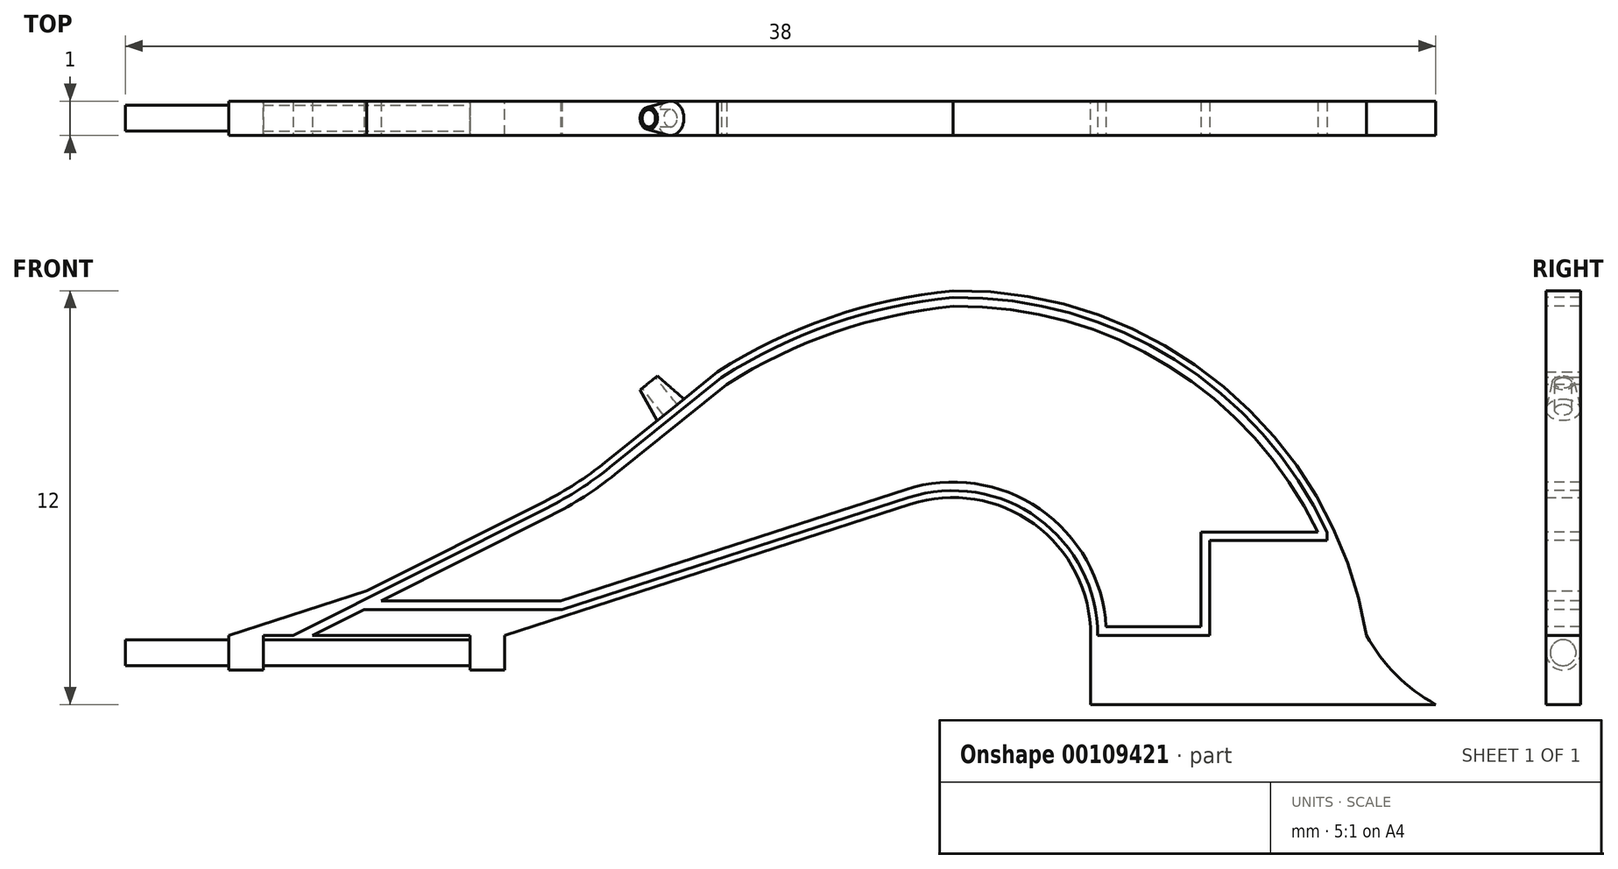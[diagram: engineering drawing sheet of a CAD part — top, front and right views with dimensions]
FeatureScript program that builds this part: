
annotation { "Feature Type Name" : "Feature", "Feature Type Description" : "" }
export const myFeature = defineFeature(function(context is Context, id is Id, definition is map)
    precondition{}
    {
        {
            var Q0;
            Q0=qCreatedBy(makeId("Front.planeOp"),FACE);
            var sketch = newSketch(context, id + "F0", { "sketchPlane" : qUnion([Q0])});
            skArc(sketch, "E0", {"start": v(4, 0) * mm, "mid": v(2.35, 3.23) * mm, "end": v(-1.23, 3.8) * mm});
            skLineSegment(sketch, "E1", {"start": v(-13, 0) * mm, "end": v(-1.23, 3.8) * mm});
            skLineSegment(sketch, "E2", {"start": v(-13, 0) * mm, "end": v(-21, 0) * mm});
            skLineSegment(sketch, "E3", {"start": v(-21, 0) * mm, "end": v(-17, 1.3) * mm});
            skArc(sketch, "E4", {"start": v(12, 0) * mm, "mid": v(7.85, 7.22) * mm, "end": v(0, 10) * mm});
            skLineSegment(sketch, "E5.left", {"start": v(4, 0) * mm, "end": v(4, -2) * mm});
            skPoint(sketch, "E6.visualSharp", {"position": v(-17, 1.3) * mm});
            skArc(sketch, "E7", {"start": v(12, 0) * mm, "mid": v(12.86, -1.14) * mm, "end": v(14, -2) * mm});
            skLineSegment(sketch, "E8", {"start": v(4, -2) * mm, "end": v(14, -2) * mm});
            skLineSegment(sketch, "E9", {"start": v(-17, 1.3) * mm, "end": v(-11.86, 3.88) * mm});
            skLineSegment(sketch, "E10", {"start": v(-10.08, 5.03) * mm, "end": v(-6.83, 7.65) * mm});
            skPoint(sketch, "E11.visualSharp", {"position": v(-10.9, 4.36) * mm});
            skArc(sketch, "E11.filletArc", {"start": v(-11.86, 3.88) * mm, "mid": v(-10.94, 4.4) * mm, "end": v(-10.08, 5.03) * mm});
            skArc(sketch, "E12", {"start": v(0, 10) * mm, "mid": v(-3.55, 9.23) * mm, "end": v(-6.83, 7.65) * mm});
            skSolve(sketch);
        }
        {
            var Q0;
            Q0 = qSketchRegion(id + "F0", true);
            extrude(context, id + "F1", {"entities" : qUnion([Q0]), "depth" : 1 * mm, "offsetDistance" : 25 * mm});
        }
        {
            var Q0;
            Q0=makeQuery(id+"F1.opExtrude","SWEPT_FACE",FACE,{"disambiguationData":[OSD([sQuery(id+"F0.wireOp",EDGE,"E2")])]});
            var sketch = newSketch(context, id + "F2", { "sketchPlane" : qUnion([Q0])});
            skLineSegment(sketch, "E13.bottom", {"start": v(-13, 1) * mm, "end": v(-14, 1) * mm});
            skLineSegment(sketch, "E13.top", {"start": v(-13, 0) * mm, "end": v(-14, 0) * mm});
            skLineSegment(sketch, "E13.left", {"start": v(-13, 1) * mm, "end": v(-13, 0) * mm});
            skLineSegment(sketch, "E13.right", {"start": v(-14, 1) * mm, "end": v(-14, 0) * mm});
            skSolve(sketch);
        }
        {
            var Q0;
            Q0 = qSketchRegion(id + "F2", true);
            extrude(context, id + "F3", {"entities" : qUnion([Q0]), "operationType" : NewBodyOperationType.ADD, "depth" : 1 * mm});
        }
        {
            var Q0;
            Q0=makeQuery(id+"F3.opExtrude","SWEPT_FACE",FACE,{"disambiguationData":[OSD([sQuery(id+"F2.wireOp",EDGE,"E13.right")])]});
            var sketch = newSketch(context, id + "F4", { "sketchPlane" : qUnion([Q0])});
            skLineSegment(sketch, "E14.top", {"start": v(0.5, -1) * mm, "end": v(0.5, -1) * mm});
            skLineSegment(sketch, "E14.left", {"start": v(0, 0) * mm, "end": v(0, -0.5) * mm});
            skLineSegment(sketch, "E14.right", {"start": v(1, 0) * mm, "end": v(1, -0.5) * mm});
            skPoint(sketch, "E15.visualSharp", {"position": v(0, -1) * mm});
            skArc(sketch, "E15.filletArc", {"start": v(0, -0.5) * mm, "mid": v(0.15, -0.85) * mm, "end": v(0.5, -1) * mm});
            skPoint(sketch, "E16.visualSharp", {"position": v(1, -1) * mm});
            skArc(sketch, "E16.filletArc", {"start": v(0.5, -1) * mm, "mid": v(0.85, -0.85) * mm, "end": v(1, -0.5) * mm});
            skLineSegment(sketch, "E17", {"start": v(0, 0) * mm, "end": v(-0.43, 0) * mm});
            skLineSegment(sketch, "E18", {"start": v(-0.43, 0) * mm, "end": v(-0.43, -1) * mm});
            skLineSegment(sketch, "E19", {"start": v(1, 0) * mm, "end": v(1.47, 0) * mm});
            skLineSegment(sketch, "E20", {"start": v(1.47, 0) * mm, "end": v(1.47, -1) * mm});
            skLineSegment(sketch, "E21", {"start": v(-0.43, -1) * mm, "end": v(0.5, -1.26) * mm});
            skLineSegment(sketch, "E22", {"start": v(0.5, -1.26) * mm, "end": v(1.47, -1) * mm});
            skLineSegment(sketch, "E23", {"start": v(1, -0.5) * mm, "end": v(1, 0) * mm});
            skLineSegment(sketch, "E24", {"start": v(0, -0.5) * mm, "end": v(0, 0) * mm});
            skSolve(sketch);
        }
        {
            var Q0;
            Q0 = qSketchRegion(id + "F4", true);
            extrude(context, id + "F5", {"entities" : qUnion([Q0]), "operationType" : NewBodyOperationType.REMOVE, "oppositeDirection" : true, "depth" : 1.1 * mm});
        }
        {
            var Q0;
            Q0=makeQuery(id+"F3.opExtrude","SWEPT_FACE",FACE,{"disambiguationData":[OSD([sQuery(id+"F2.wireOp",EDGE,"E13.right")])]});
            var sketch = newSketch(context, id + "F6", { "sketchPlane" : qUnion([Q0])});
            skCircle(sketch, "E25", {"center": v(0.5, -0.5) * mm, "radius": 0.5 * mm});
            skSolve(sketch);
        }
        {
            var Q0;
            Q0 = qSketchRegion(id + "F6", true);
            extrude(context, id + "F7", {"entities" : qUnion([Q0]), "depth" : 10 * mm});
        }
        {
            var Q0;
            Q0=makeQuery(id+"F1.opExtrude","SWEPT_FACE",FACE,{"disambiguationData":[OSD([sQuery(id+"F0.wireOp",EDGE,"E10")])]});
            var sketch = newSketch(context, id + "F8", { "sketchPlane" : qUnion([Q0])});
            skCircle(sketch, "E26", {"center": v(-2.27, -0.5) * mm, "radius": 0.5 * mm});
            skSolve(sketch);
        }
        {
            var Q0;
            Q0 = qSketchRegion(id + "F8", true);
            extrude(context, id + "F9", {"entities" : qUnion([Q0]), "operationType" : NewBodyOperationType.ADD, "depth" : 1 * mm, "hasDraft" : true, "draftAngle" : 10 * degree, "draftPullDirection" : true});
        }
        {
            var Q0;
            Q0=makeQuery(id+"F9.opExtrude","CAP_FACE",FACE,{"disambiguationData":[OSD([sQuery(id+"F8.wireOp",EDGE,"E26")])],"isStart":false});
            var sketch = newSketch(context, id + "F10", { "sketchPlane" : qUnion([Q0])});
            skCircle(sketch, "E27", {"center": v(-2.27, -0.5) * mm, "radius": 0.25 * mm});
            skSolve(sketch);
        }
        {
            var Q0;
            Q0=makeQuery(id+"F10.imprint","IMPRINT",FACE,{"disambiguationData":[TD([[makeQuery(id+"F10.imprint","IMPRINT",EDGE,{"derivedFrom":sQuery(id+"F10.wireOp",EDGE,"E27")}),1.0]])]});
            extrude(context, id + "F11", {"entities" : qUnion([Q0]), "operationType" : NewBodyOperationType.REMOVE, "oppositeDirection" : true, "depth" : 1 * mm});
        }
        {
            var Q0;
            Q0=makeQuery(id+"F7.opExtrude","SWEPT_BODY",BODY,{"disambiguationData":[OSD([sQuery(id+"F6.wireOp",EDGE,"E25")])]});
            deleteBodies(context, id + "F12", {"entities" : qUnion([Q0])});
        }
        {
            var Q0;
            Q0=makeQuery(id+"F3.opExtrude","SWEPT_FACE",FACE,{"disambiguationData":[OSD([sQuery(id+"F2.wireOp",EDGE,"E13.right")])]});
            var sketch = newSketch(context, id + "F13", { "sketchPlane" : qUnion([Q0])});
            skCircle(sketch, "E28", {"center": v(0.5, -0.5) * mm, "radius": 0.38 * mm});
            skSolve(sketch);
        }
        {
            var Q0;
            Q0 = qSketchRegion(id + "F13", true);
            extrude(context, id + "F14", {"entities" : qUnion([Q0]), "operationType" : NewBodyOperationType.ADD, "depth" : 10 * mm});
        }
        {
            var Q0;
            Q0=makeQuery(id+"F1.opExtrude","SWEPT_FACE",FACE,{"disambiguationData":[OSD([sQuery(id+"F0.wireOp",EDGE,"E2")])]});
            var sketch = newSketch(context, id + "F15", { "sketchPlane" : qUnion([Q0])});
            skLineSegment(sketch, "E29.bottom", {"start": v(-21, 0) * mm, "end": v(-20, 0) * mm});
            skLineSegment(sketch, "E29.top", {"start": v(-21, 1) * mm, "end": v(-20, 1) * mm});
            skLineSegment(sketch, "E29.left", {"start": v(-21, 0) * mm, "end": v(-21, 1) * mm});
            skLineSegment(sketch, "E29.right", {"start": v(-20, 0) * mm, "end": v(-20, 1) * mm});
            skSolve(sketch);
        }
        {
            var Q0;
            Q0 = qSketchRegion(id + "F15", true);
            extrude(context, id + "F16", {"entities" : qUnion([Q0]), "operationType" : NewBodyOperationType.ADD, "depth" : 1 * mm});
        }
        {
            var Q0;
            Q0=makeQuery(id+"F16.opExtrude","SWEPT_FACE",FACE,{"disambiguationData":[OSD([sQuery(id+"F15.wireOp",EDGE,"E29.right")])]});
            var sketch = newSketch(context, id + "F17", { "sketchPlane" : qUnion([Q0])});
            skArc(sketch, "E30", {"start": v(-1, -0.5) * mm, "mid": v(-0.5, -1) * mm, "end": v(0, -0.5) * mm});
            skLineSegment(sketch, "E31", {"start": v(0, -0.5) * mm, "end": v(0, -1) * mm});
            skLineSegment(sketch, "E32", {"start": v(0, -1) * mm, "end": v(-1, -1) * mm});
            skLineSegment(sketch, "E33", {"start": v(-1, -1) * mm, "end": v(-1, -0.5) * mm});
            skSolve(sketch);
        }
        {
            var Q0;
            Q0 = qSketchRegion(id + "F17", true);
            extrude(context, id + "F18", {"entities" : qUnion([Q0]), "operationType" : NewBodyOperationType.REMOVE, "oppositeDirection" : true, "depth" : 25 * mm});
        }
        {
            var Q0;
            Q0=makeQuery(id+"F16.boolean.opBoolean","MERGE",FACE,{"derivedFrom":[makeQuery(id+"F3.boolean.opBoolean","MERGE",FACE,{"derivedFrom":[makeQuery(id+"F1.opExtrude","CAP_FACE",FACE,{"disambiguationData":[OSD([sQuery(id+"F0.wireOp",EDGE,"E0"),sQuery(id+"F0.wireOp",EDGE,"E1"),sQuery(id+"F0.wireOp",EDGE,"E2"),sQuery(id+"F0.wireOp",EDGE,"E3"),sQuery(id+"F0.wireOp",EDGE,"E4"),sQuery(id+"F0.wireOp",EDGE,"E5.left"),sQuery(id+"F0.wireOp",EDGE,"E7"),sQuery(id+"F0.wireOp",EDGE,"E8"),sQuery(id+"F0.wireOp",EDGE,"E9"),sQuery(id+"F0.wireOp",EDGE,"E10"),sQuery(id+"F0.wireOp",EDGE,"E11.filletArc"),sQuery(id+"F0.wireOp",EDGE,"E12")])],"isStart":false}),makeQuery(id+"F3.opExtrude","SWEPT_FACE",FACE,{"disambiguationData":[OSD([sQuery(id+"F2.wireOp",EDGE,"E13.bottom")])]})]}),makeQuery(id+"F16.opExtrude","SWEPT_FACE",FACE,{"disambiguationData":[OSD([sQuery(id+"F15.wireOp",EDGE,"E29.top")])]})]});
            var sketch = newSketch(context, id + "F19", { "sketchPlane" : qUnion([Q0])});
            skLineSegment(sketch, "E34.0", {"start": v(-19.13, 0) * mm, "end": v(-11.77, 3.7) * mm});
            skArc(sketch, "E34.1", {"start": v(-11.77, 3.7) * mm, "mid": v(-10.83, 4.24) * mm, "end": v(-9.95, 4.87) * mm});
            skArc(sketch, "E34.2", {"start": v(10.86, 3) * mm, "mid": v(6.44, 8) * mm, "end": v(0.01, 9.8) * mm});
            skArc(sketch, "E34.3", {"start": v(0.01, 9.8) * mm, "mid": v(-3.49, 9.04) * mm, "end": v(-6.71, 7.48) * mm});
            skLineSegment(sketch, "E34.4", {"start": v(-7.96, 6.47) * mm, "end": v(-6.71, 7.48) * mm});
            skLineSegment(sketch, "E34.5", {"start": v(-9.95, 4.87) * mm, "end": v(-7.96, 6.47) * mm});
            skArc(sketch, "E35.0", {"start": v(10.58, 3) * mm, "mid": v(6.26, 7.81) * mm, "end": v(0.02, 9.55) * mm});
            skArc(sketch, "E35.1", {"start": v(0.02, 9.55) * mm, "mid": v(-3.4, 8.8) * mm, "end": v(-6.57, 7.28) * mm});
            skLineSegment(sketch, "E35.2", {"start": v(-18.57, 0) * mm, "end": v(-17.08, 0.75) * mm});
            skArc(sketch, "E35.3", {"start": v(-11.66, 3.48) * mm, "mid": v(-10.7, 4.03) * mm, "end": v(-9.8, 4.68) * mm});
            skLineSegment(sketch, "E35.4", {"start": v(-9.8, 4.68) * mm, "end": v(-7.57, 6.47) * mm});
            skLineSegment(sketch, "E35.5", {"start": v(-7.57, 6.47) * mm, "end": v(-6.57, 7.28) * mm});
            skLineSegment(sketch, "E36.0", {"start": v(-11.33, 0.75) * mm, "end": v(-1.3, 4) * mm});
            skArc(sketch, "E37.0", {"start": v(4.2, 0) * mm, "mid": v(2.47, 3.4) * mm, "end": v(-1.3, 4) * mm});
            skLineSegment(sketch, "E38.0", {"start": v(-11.37, 1) * mm, "end": v(-1.37, 4.23) * mm});
            skArc(sketch, "E39.0", {"start": v(4.44, 0.25) * mm, "mid": v(2.52, 3.67) * mm, "end": v(-1.37, 4.23) * mm});
            skLineSegment(sketch, "E40", {"start": v(-11.37, 1) * mm, "end": v(-16.58, 1) * mm});
            skLineSegment(sketch, "E41", {"start": v(-11.33, 0.75) * mm, "end": v(-17.08, 0.75) * mm});
            skLineSegment(sketch, "E42", {"start": v(-19.13, 0) * mm, "end": v(-18.57, 0) * mm});
            skLineSegment(sketch, "E43", {"start": v(4.2, 0) * mm, "end": v(7.44, 0) * mm});
            skLineSegment(sketch, "E44", {"start": v(7.44, 0) * mm, "end": v(7.44, 2.75) * mm});
            skLineSegment(sketch, "E45", {"start": v(7.44, 2.75) * mm, "end": v(10.86, 2.75) * mm});
            skLineSegment(sketch, "E46", {"start": v(4.44, 0.25) * mm, "end": v(7.2, 0.25) * mm});
            skLineSegment(sketch, "E47", {"start": v(7.2, 0.25) * mm, "end": v(7.2, 3) * mm});
            skLineSegment(sketch, "E48", {"start": v(7.2, 3) * mm, "end": v(10.58, 3) * mm});
            skLineSegment(sketch, "E49", {"start": v(10.86, 2.75) * mm, "end": v(10.86, 3) * mm});
            skLineSegment(sketch, "E50.trimOffspring", {"start": v(-16.58, 1) * mm, "end": v(-11.66, 3.48) * mm});
            skSolve(sketch);
        }
        {
            var Q0;
            Q0 = qSketchRegion(id + "F19", true);
            extrude(context, id + "F20", {"entities" : qUnion([Q0]), "operationType" : NewBodyOperationType.REMOVE, "oppositeDirection" : true, "depth" : 20 * mm});
        }
    });
